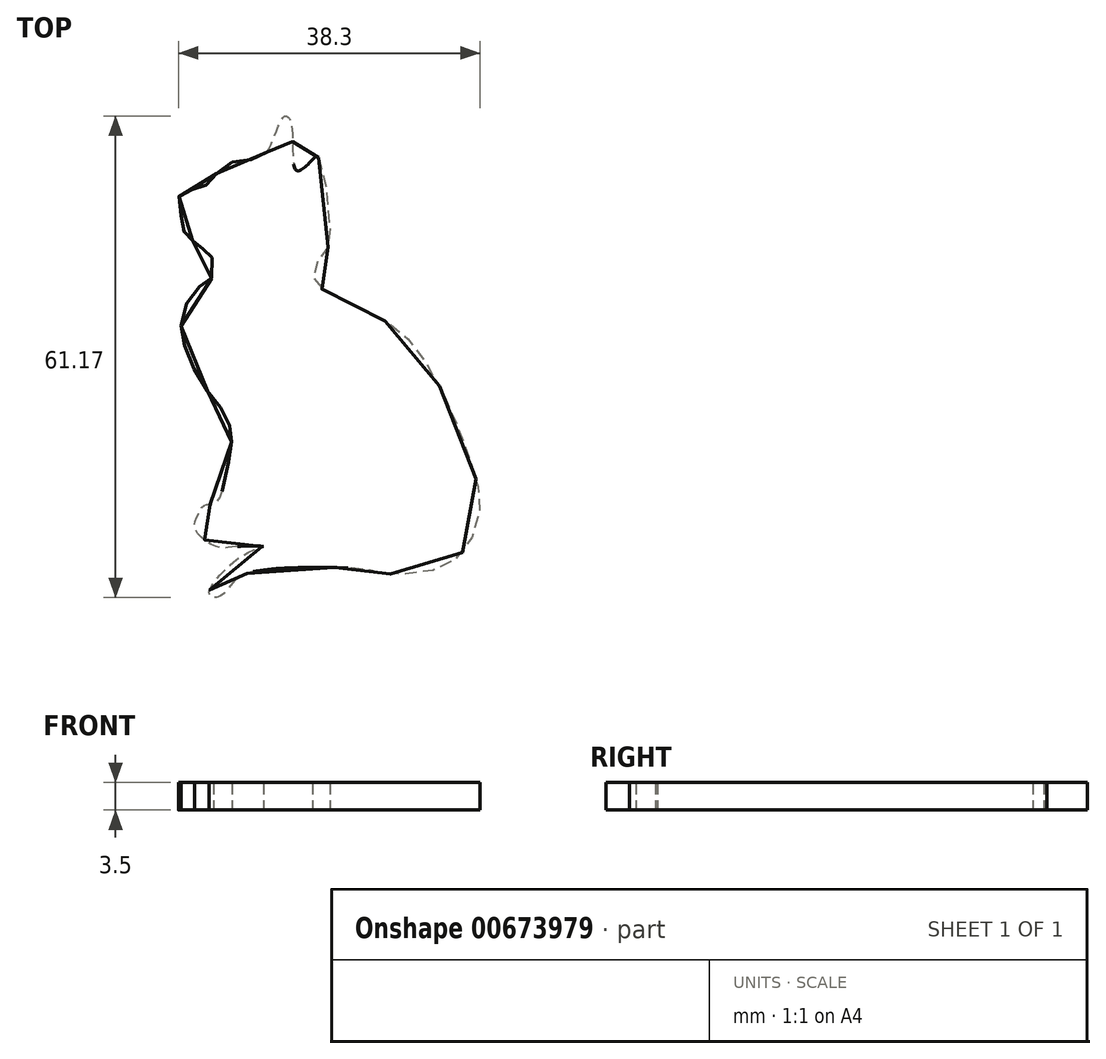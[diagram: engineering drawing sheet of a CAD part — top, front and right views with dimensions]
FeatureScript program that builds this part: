
annotation { "Feature Type Name" : "Feature", "Feature Type Description" : "" }
export const myFeature = defineFeature(function(context is Context, id is Id, definition is map)
    precondition{}
    {
        {
            var Q0;
            Q0=qCreatedBy(makeId("Top.planeOp"),FACE);
            var sketch = newSketch(context, id + "F0", { "sketchPlane" : qUnion([Q0])});
            skFitSpline(sketch, "E0", {"points": [v(-34.2, 57.1) * mm, v(-32.74, 46.88) * mm, v(-33.22, 45.42) * mm, v(-34.77, 43.07) * mm, v(-34.52, 41.04) * mm, v(-31.44, 39.25) * mm, v(-26.81, 36.98) * mm, v(-22.75, 33.98) * mm, v(-17.96, 26.26) * mm, v(-14.47, 17.17) * mm, v(-13.74, 12.06) * mm, v(-16.42, 6.38) * mm, v(-21.37, 4.35) * mm, v(-26.65, 4.35) * mm, v(-28.03, 4.76) * mm, v(-31.92, 5) * mm, v(-40.2, 4.84) * mm, v(-44.75, 3.46) * mm, v(-46.7, 1.35) * mm, v(-48.07, 1.67) * mm, v(-43.29, 6.87) * mm, v(-41.18, 7.68) * mm, v(-44.75, 7.68) * mm, v(-46.94, 7.6) * mm, v(-49.86, 9.87) * mm, v(-49.45, 11.82) * mm, v(-48.64, 12.95) * mm, v(-47.18, 13.28) * mm, v(-45.48, 19.28) * mm, v(-45.23, 21.88) * mm, v(-46.29, 24.8) * mm, v(-48.72, 28.05) * mm, v(-51.16, 33.08) * mm, v(-51.57, 36.73) * mm, v(-49.46, 40.63) * mm, v(-47.83, 41.69) * mm, v(-47.91, 44.85) * mm, v(-48.89, 45.5) * mm, v(-50.19, 46.56) * mm, v(-51.16, 47.45) * mm, v(-51.57, 49.4) * mm, v(-51.81, 52.4) * mm, v(-49.78, 53.13) * mm, v(-48.24, 53.78) * mm, v(-46.62, 55.65) * mm, v(-43.53, 56.86) * mm, v(-41.02, 57.43) * mm, v(-38.58, 62.3) * mm, v(-37.69, 61.49) * mm, v(-37.04, 55.48) * mm, v(-35.17, 56.62) * mm, v(-34.2, 57.1) * mm]});
            skSolve(sketch);
        }
        {
            var Q0;
            Q0=makeQuery(id+"F0.imprint","IMPRINT",FACE,{"disambiguationData":[TD([[makeQuery(id+"F0.imprint","IMPRINT",EDGE,{"derivedFrom":sQuery(id+"F0.wireOp",EDGE,"E0")}),-1.0]])]});
            extrude(context, id + "F1", {"entities" : qUnion([Q0]), "depth" : 3.5 * mm, "offsetDistance" : 25 * mm});
        }
    });
